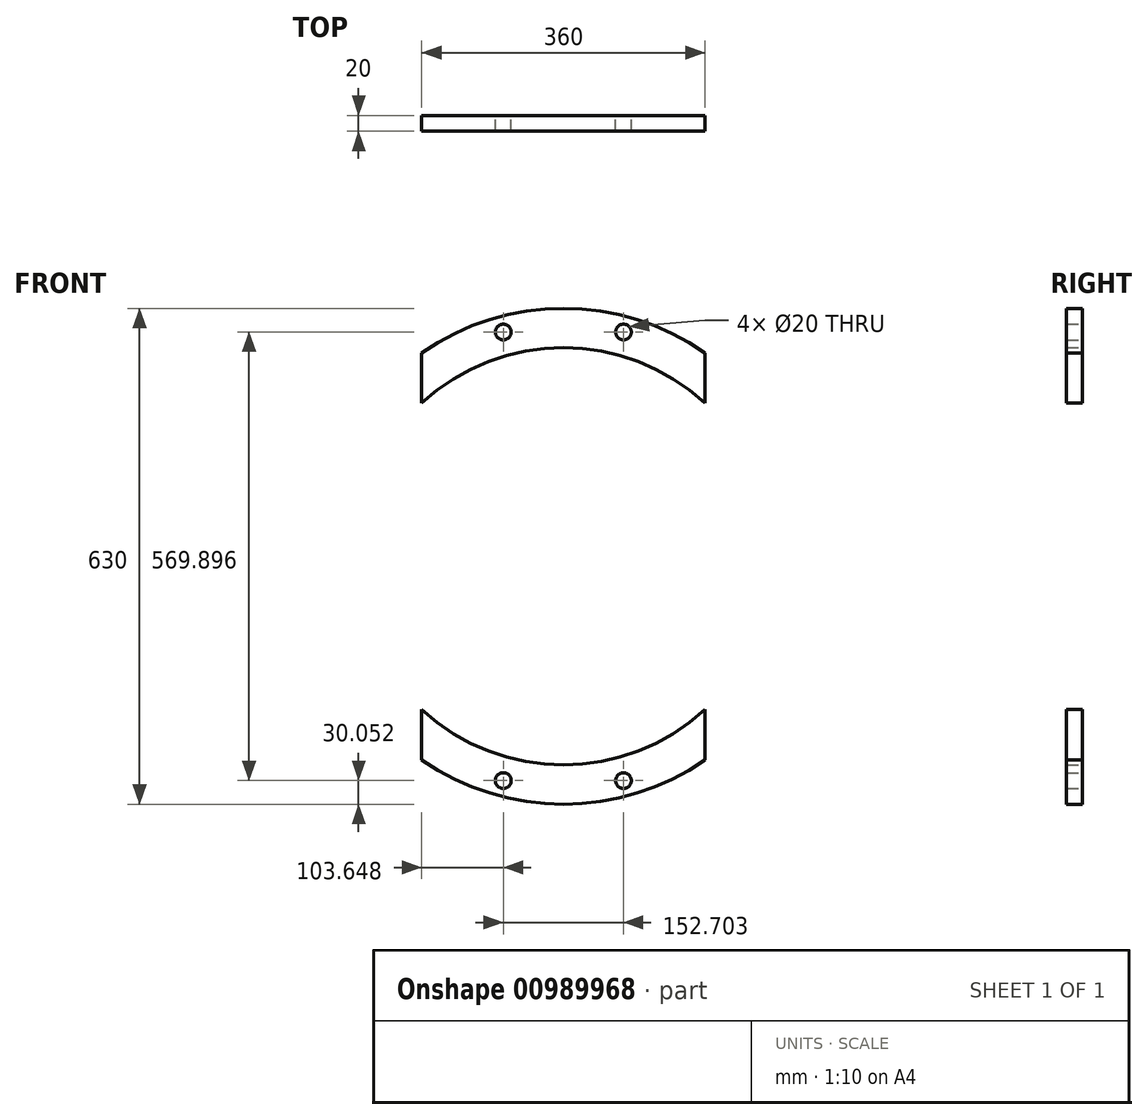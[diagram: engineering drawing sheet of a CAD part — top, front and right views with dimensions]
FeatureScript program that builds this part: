
annotation { "Feature Type Name" : "Feature", "Feature Type Description" : "" }
export const myFeature = defineFeature(function(context is Context, id is Id, definition is map)
    precondition{}
    {
        {
            var Q0;
            Q0=qCreatedBy(makeId("Front.planeOp"),FACE);
            var sketch = newSketch(context, id + "F0", { "sketchPlane" : qUnion([Q0])});
            skCircle(sketch, "E0", {"center": v(0, 0) * mm, "radius": 265 * mm});
            skCircle(sketch, "E1", {"center": v(0, 0) * mm, "radius": 315 * mm});
            skCircle(sketch, "E2", {"center": v(0, 0) * mm, "radius": 295 * mm, "construction": true});
            skCircle(sketch, "E3.2.0", {"center": v(-208.6, -208.6) * mm, "radius": 10 * mm});
            skCircle(sketch, "E4.1.0", {"center": v(-76.35, -284.95) * mm, "radius": 10 * mm});
            skCircle(sketch, "E4.2.0", {"center": v(76.35, -284.95) * mm, "radius": 10 * mm});
            skCircle(sketch, "E4.3.0", {"center": v(208.6, -208.6) * mm, "radius": 10 * mm});
            skCircle(sketch, "E4.4.0", {"center": v(284.95, -76.35) * mm, "radius": 10 * mm});
            skCircle(sketch, "E4.5.0", {"center": v(284.95, 76.35) * mm, "radius": 10 * mm});
            skCircle(sketch, "E4.6.0", {"center": v(208.6, 208.6) * mm, "radius": 10 * mm});
            skCircle(sketch, "E4.7.0", {"center": v(76.35, 284.95) * mm, "radius": 10 * mm});
            skCircle(sketch, "E4.8.0", {"center": v(-76.35, 284.95) * mm, "radius": 10 * mm});
            skCircle(sketch, "E4.9.0", {"center": v(-208.6, 208.6) * mm, "radius": 10 * mm});
            skCircle(sketch, "E4.10.0", {"center": v(-284.95, 76.35) * mm, "radius": 10 * mm});
            skCircle(sketch, "E4.11.0", {"center": v(-284.95, -76.35) * mm, "radius": 10 * mm});
            skLineSegment(sketch, "E5.bottom", {"start": v(-180, 358.5) * mm, "end": v(180, 358.5) * mm});
            skLineSegment(sketch, "E5.top", {"start": v(-180, -360.5) * mm, "end": v(180, -360.5) * mm});
            skLineSegment(sketch, "E5.left", {"start": v(-180, 358.5) * mm, "end": v(-180, -360.5) * mm});
            skLineSegment(sketch, "E5.right", {"start": v(180, 358.5) * mm, "end": v(180, -360.5) * mm});
            skSolve(sketch);
        }
        {
            var Q0;
            Q0=makeQuery(id+"F0.imprint","IMPRINT",FACE,{"disambiguationData":[TD([[makeQuery(id+"F0.imprint","IMPRINT",EDGE,{"derivedFrom":sQuery(id+"F0.wireOp",EDGE,"E0")}),-1.0]])]});
            extrude(context, id + "F1", {"entities" : qUnion([Q0]), "depth" : 20 * mm, "offsetDistance" : 25 * mm});
        }
    });
